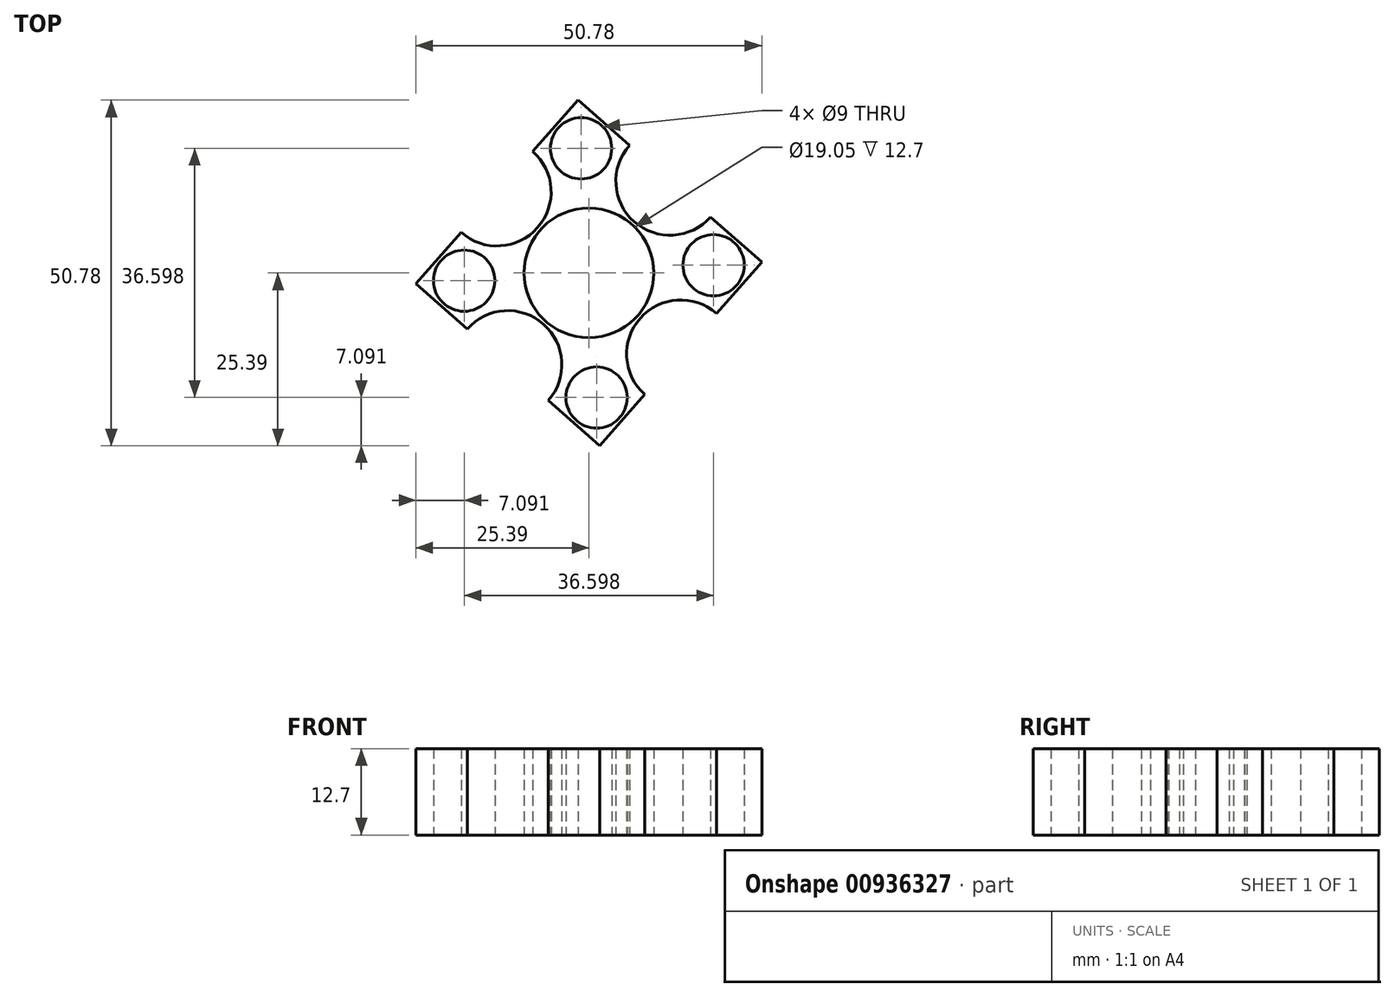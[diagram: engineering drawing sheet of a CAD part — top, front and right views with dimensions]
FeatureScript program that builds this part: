
annotation { "Feature Type Name" : "Feature", "Feature Type Description" : "" }
export const myFeature = defineFeature(function(context is Context, id is Id, definition is map)
    precondition{}
    {
        {
            var Q0;
            Q0=qCreatedBy(makeId("Top.planeOp"),FACE);
            var sketch = newSketch(context, id + "F0", { "sketchPlane" : qUnion([Q0])});
            skLineSegment(sketch, "E0.0", {"start": v(-1.58, 25.39) * mm, "end": v(5.95, 18.74) * mm});
            skLineSegment(sketch, "E0.1", {"start": v(25.39, 1.58) * mm, "end": v(18.74, -5.95) * mm});
            skLineSegment(sketch, "E0.2", {"start": v(1.58, -25.39) * mm, "end": v(-5.95, -18.74) * mm});
            skLineSegment(sketch, "E0.3", {"start": v(-25.39, -1.58) * mm, "end": v(-18.74, 5.95) * mm});
            skArc(sketch, "E1", {"start": v(5.95, 18.74) * mm, "mid": v(6.65, 7.53) * mm, "end": v(17.86, 8.23) * mm});
            skArc(sketch, "E2.1.0", {"start": v(18.74, -5.95) * mm, "mid": v(7.53, -6.65) * mm, "end": v(8.23, -17.86) * mm});
            skArc(sketch, "E2.2.0", {"start": v(-5.95, -18.74) * mm, "mid": v(-6.65, -7.53) * mm, "end": v(-17.86, -8.23) * mm});
            skPoint(sketch, "E2.center", {"position": v(0, 0) * mm});
            skArc(sketch, "E3.1.0", {"start": v(-18.74, 5.95) * mm, "mid": v(-7.53, 6.65) * mm, "end": v(-8.23, 17.86) * mm});
            skLineSegment(sketch, "E4.trimOffspring", {"start": v(-8.23, 17.86) * mm, "end": v(-1.58, 25.39) * mm});
            skLineSegment(sketch, "E5.trimOffspring", {"start": v(17.86, 8.23) * mm, "end": v(25.39, 1.58) * mm});
            skLineSegment(sketch, "E6.trimOffspring", {"start": v(8.23, -17.86) * mm, "end": v(1.58, -25.39) * mm});
            skLineSegment(sketch, "E7.trimOffspring", {"start": v(-17.86, -8.23) * mm, "end": v(-25.39, -1.58) * mm});
            skPoint(sketch, "E8", {"position": v(1.14, -18.3) * mm});
            skPoint(sketch, "E9", {"position": v(18.3, 1.14) * mm});
            skPoint(sketch, "E10", {"position": v(-18.3, -1.14) * mm});
            skPoint(sketch, "E11", {"position": v(-1.14, 18.3) * mm});
            skSolve(sketch);
        }
        {
            var Q0;
            Q0=makeQuery(id+"F0.imprint","IMPRINT",FACE,{"disambiguationData":[TD([[makeQuery(id+"F0.imprint","IMPRINT",EDGE,{"derivedFrom":sQuery(id+"F0.wireOp",EDGE,"E0.0")}),-1.0]])]});
            extrude(context, id + "F1", {"entities" : qUnion([Q0]), "depth" : 12.7 * mm, "offsetDistance" : 25.4 * mm});
        }
        {
            var Q0;
            Q0=sQuery(id+"F0.wireOp",VERTEX,"E2.center");
            var Q1;
            Q1=makeQuery(id+"F1.opExtrude","SWEPT_BODY",BODY,{"disambiguationData":[OSD([sQuery(id+"F0.wireOp",EDGE,"E0.0"),sQuery(id+"F0.wireOp",EDGE,"E0.1"),sQuery(id+"F0.wireOp",EDGE,"E0.2"),sQuery(id+"F0.wireOp",EDGE,"E0.3"),sQuery(id+"F0.wireOp",EDGE,"E1"),sQuery(id+"F0.wireOp",EDGE,"E2.1.0"),sQuery(id+"F0.wireOp",EDGE,"E3.1.0"),sQuery(id+"F0.wireOp",EDGE,"E2.2.0"),sQuery(id+"F0.wireOp",EDGE,"E4.trimOffspring"),sQuery(id+"F0.wireOp",EDGE,"E5.trimOffspring"),sQuery(id+"F0.wireOp",EDGE,"E6.trimOffspring"),sQuery(id+"F0.wireOp",EDGE,"E7.trimOffspring")])]});
            hole(context, id + "F2", {"style" : HoleStyle.SIMPLE, "endStyle" : HoleEndStyle.THROUGH, "oppositeDirection" : true, "holeDiameter" : 19.05 * mm, "majorDiameter" : 6.35 * mm, "isTappedThrough" : true, "tappedDepth" : 12.7 * mm, "tapClearance" : 3, "locations" : qUnion([Q0]), "scope" : qUnion([Q1])});
        }
        {
            var Q0;
            Q0=sQuery(id+"F0.wireOp",VERTEX,"E9");
            var Q1;
            Q1=sQuery(id+"F0.wireOp",VERTEX,"E11");
            var Q2;
            Q2=sQuery(id+"F0.wireOp",VERTEX,"E10");
            var Q3;
            Q3=sQuery(id+"F0.wireOp",VERTEX,"E8");
            var Q4;
            Q4=makeQuery(id+"F1.opExtrude","SWEPT_BODY",BODY,{"disambiguationData":[OSD([sQuery(id+"F0.wireOp",EDGE,"E0.0"),sQuery(id+"F0.wireOp",EDGE,"E0.1"),sQuery(id+"F0.wireOp",EDGE,"E0.2"),sQuery(id+"F0.wireOp",EDGE,"E0.3"),sQuery(id+"F0.wireOp",EDGE,"E1"),sQuery(id+"F0.wireOp",EDGE,"E2.1.0"),sQuery(id+"F0.wireOp",EDGE,"E3.1.0"),sQuery(id+"F0.wireOp",EDGE,"E2.2.0"),sQuery(id+"F0.wireOp",EDGE,"E4.trimOffspring"),sQuery(id+"F0.wireOp",EDGE,"E5.trimOffspring"),sQuery(id+"F0.wireOp",EDGE,"E6.trimOffspring"),sQuery(id+"F0.wireOp",EDGE,"E7.trimOffspring")])]});
            hole(context, id + "F3", {"style" : HoleStyle.SIMPLE, "endStyle" : HoleEndStyle.THROUGH, "oppositeDirection" : true, "holeDiameter" : 9 * mm, "majorDiameter" : 6.35 * mm, "isTappedThrough" : true, "tappedDepth" : 12.7 * mm, "tapClearance" : 3, "locations" : qUnion([Q0, Q1, Q2, Q3]), "scope" : qUnion([Q4])});
        }
    });
